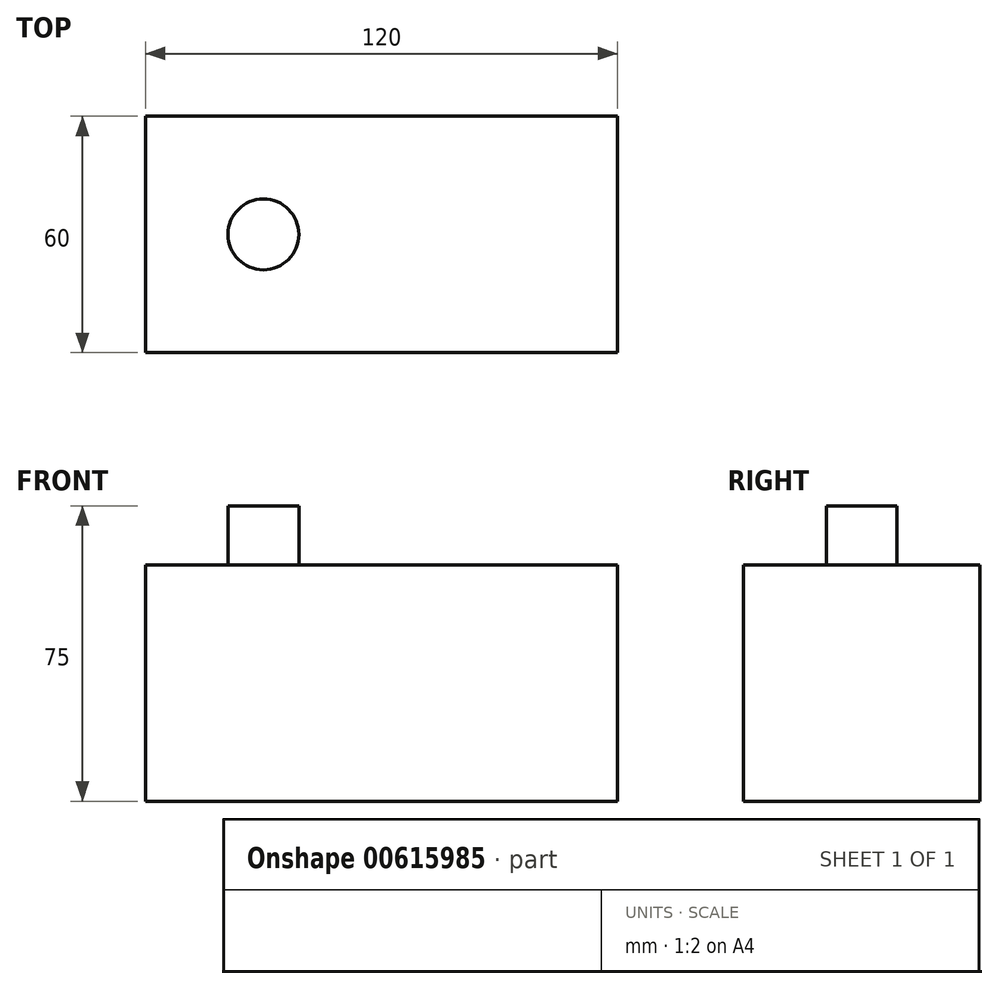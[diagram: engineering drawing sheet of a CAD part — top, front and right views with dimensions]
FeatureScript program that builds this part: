
annotation { "Feature Type Name" : "Feature", "Feature Type Description" : "" }
export const myFeature = defineFeature(function(context is Context, id is Id, definition is map)
    precondition{}
    {
        {
            var Q0;
            Q0=qCreatedBy(makeId("Front.planeOp"),FACE);
            var sketch = newSketch(context, id + "F0", { "sketchPlane" : qUnion([Q0])});
            skLineSegment(sketch, "E0.bottom", {"start": v(0, 0) * mm, "end": v(120, 0) * mm});
            skLineSegment(sketch, "E0.top", {"start": v(0, 60) * mm, "end": v(120, 60) * mm});
            skLineSegment(sketch, "E0.left", {"start": v(0, 0) * mm, "end": v(0, 60) * mm});
            skLineSegment(sketch, "E0.right", {"start": v(120, 0) * mm, "end": v(120, 60) * mm});
            skSolve(sketch);
        }
        {
            var Q0;
            Q0=makeQuery(id+"F0.imprint","IMPRINT",FACE,{"disambiguationData":[TD([[makeQuery(id+"F0.imprint","IMPRINT",EDGE,{"derivedFrom":sQuery(id+"F0.wireOp",EDGE,"E0.bottom")}),1.0]])]});
            extrude(context, id + "F1", {"entities" : qUnion([Q0]), "endBound" : BoundingType.SYMMETRIC, "depth" : 60 * mm, "offsetDistance" : 25 * mm});
        }
        {
            var Q0;
            Q0=makeQuery(id+"F1.opExtrude","SWEPT_FACE",FACE,{"disambiguationData":[OSD([sQuery(id+"F0.wireOp",EDGE,"E0.top")])]});
            var sketch = newSketch(context, id + "F2", { "sketchPlane" : qUnion([Q0])});
            skLineSegment(sketch, "E1", {"start": v(0, 0) * mm, "end": v(120, 0) * mm, "construction": true});
            skLineSegment(sketch, "E2", {"start": v(30, 30) * mm, "end": v(30, -30) * mm, "construction": true});
            skLineSegment(sketch, "E3", {"start": v(60, 30) * mm, "end": v(60, -30) * mm, "construction": true});
            skCircle(sketch, "E4", {"center": v(30, 0) * mm, "radius": 9 * mm});
            skSolve(sketch);
        }
        {
            var Q0;
            Q0 = qSketchRegion(id + "F2", true);
            extrude(context, id + "F3", {"entities" : qUnion([Q0]), "operationType" : NewBodyOperationType.ADD, "depth" : 15 * mm, "offsetDistance" : 25 * mm});
        }
    });
